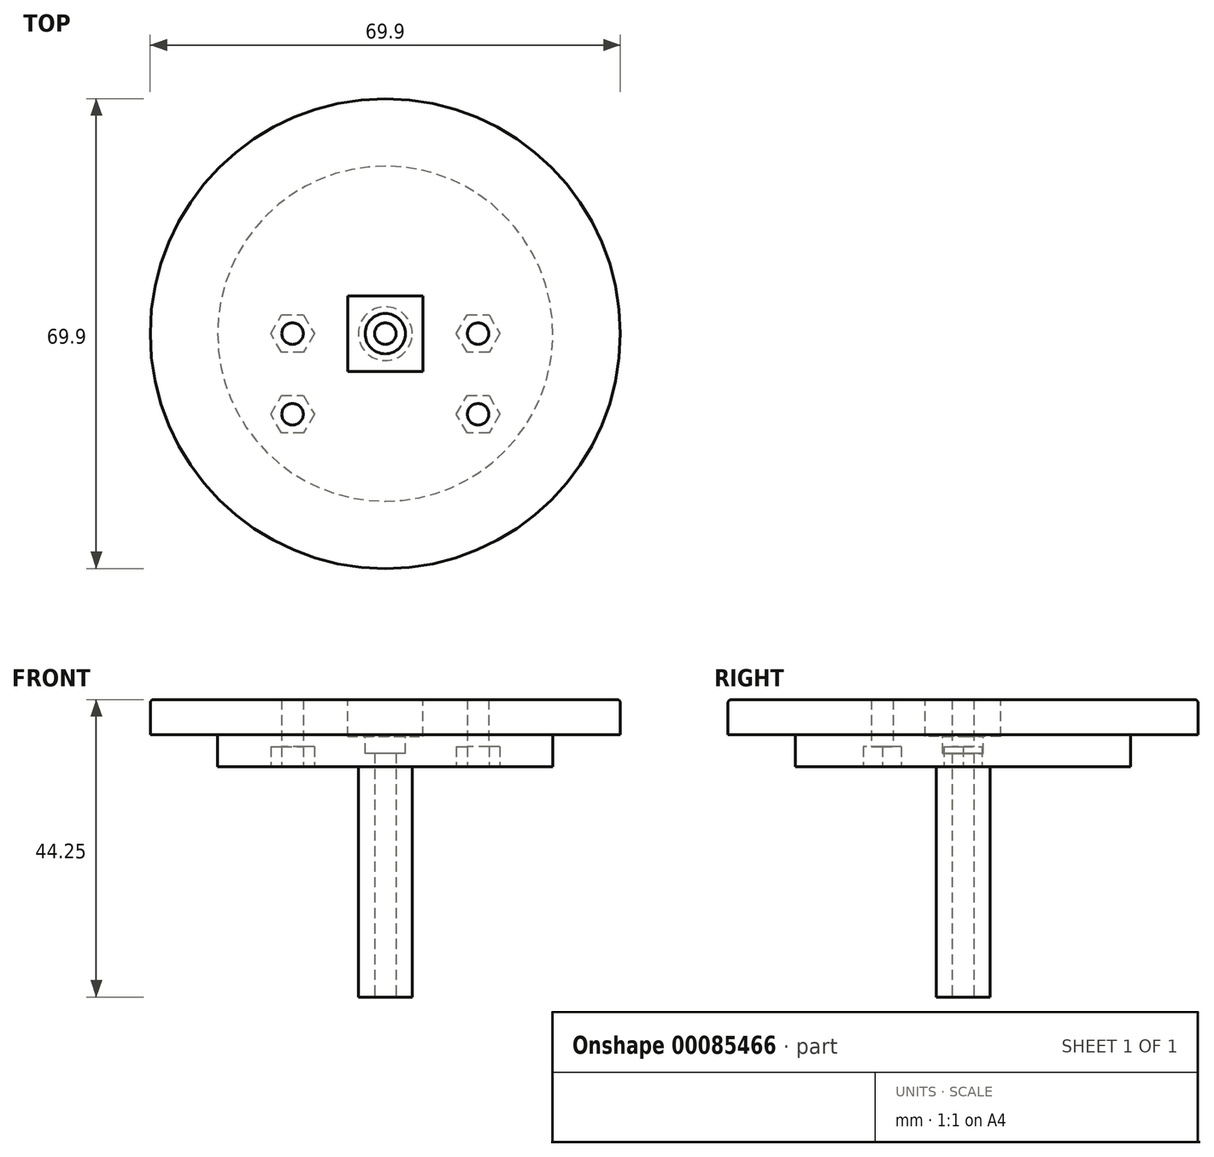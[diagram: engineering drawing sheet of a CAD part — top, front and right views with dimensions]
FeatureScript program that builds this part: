
annotation { "Feature Type Name" : "Feature", "Feature Type Description" : "" }
export const myFeature = defineFeature(function(context is Context, id is Id, definition is map)
    precondition{}
    {
        {
            var Q0;
            Q0=qCreatedBy(makeId("Top.planeOp"),FACE);
            var sketch = newSketch(context, id + "F0", { "sketchPlane" : qUnion([Q0])});
            skCircle(sketch, "E0", {"center": v(30.33, -8.57) * mm, "radius": 34.95 * mm});
            skLineSegment(sketch, "E1.bottom", {"start": v(35.93, -14.17) * mm, "end": v(24.73, -14.17) * mm});
            skLineSegment(sketch, "E1.top", {"start": v(35.93, -2.97) * mm, "end": v(24.73, -2.97) * mm});
            skLineSegment(sketch, "E1.left", {"start": v(35.93, -14.17) * mm, "end": v(35.93, -2.97) * mm});
            skLineSegment(sketch, "E1.right", {"start": v(24.73, -14.17) * mm, "end": v(24.73, -2.97) * mm});
            skPoint(sketch, "E2", {"position": v(24.73, -2.97) * mm});
            skLineSegment(sketch, "E3", {"start": v(30.33, -8.57) * mm, "end": v(5.62, -33.29) * mm, "construction": true});
            skLineSegment(sketch, "E4", {"start": v(30.33, -8.57) * mm, "end": v(55.05, 16.14) * mm, "construction": true});
            skCircle(sketch, "E5", {"center": v(30.33, -8.57) * mm, "radius": 24.93 * mm});
            skLineSegment(sketch, "E6", {"start": v(24.73, -14.17) * mm, "end": v(24.73, -43.07) * mm, "construction": true});
            skLineSegment(sketch, "E7", {"start": v(35.93, -14.17) * mm, "end": v(35.93, -43.07) * mm, "construction": true});
            skPoint(sketch, "E8", {"position": v(16.53, -20.57) * mm});
            skPoint(sketch, "E9", {"position": v(16.53, -8.57) * mm});
            skPoint(sketch, "E10", {"position": v(44.13, -8.57) * mm});
            skPoint(sketch, "E11", {"position": v(44.13, -20.57) * mm});
            skCircle(sketch, "E12.cCircle", {"center": v(16.53, -20.57) * mm, "radius": 3.23 * mm, "construction": true});
            skLineSegment(sketch, "E12.0", {"start": v(19.77, -20.57) * mm, "end": v(18.15, -23.37) * mm});
            skLineSegment(sketch, "E12.1", {"start": v(18.15, -23.37) * mm, "end": v(14.92, -23.37) * mm});
            skLineSegment(sketch, "E12.2", {"start": v(14.92, -23.37) * mm, "end": v(13.3, -20.57) * mm});
            skLineSegment(sketch, "E12.3", {"start": v(13.3, -20.57) * mm, "end": v(14.92, -17.77) * mm});
            skLineSegment(sketch, "E12.4", {"start": v(14.92, -17.77) * mm, "end": v(18.15, -17.77) * mm});
            skLineSegment(sketch, "E12.5", {"start": v(18.15, -17.77) * mm, "end": v(19.77, -20.57) * mm});
            skCircle(sketch, "E13.cCircle", {"center": v(16.53, -8.57) * mm, "radius": 3.23 * mm, "construction": true});
            skLineSegment(sketch, "E13.0", {"start": v(13.3, -8.57) * mm, "end": v(14.92, -5.77) * mm});
            skLineSegment(sketch, "E13.1", {"start": v(14.92, -5.77) * mm, "end": v(18.15, -5.77) * mm});
            skLineSegment(sketch, "E13.2", {"start": v(18.15, -5.77) * mm, "end": v(19.77, -8.57) * mm});
            skLineSegment(sketch, "E13.3", {"start": v(19.77, -8.57) * mm, "end": v(18.15, -11.37) * mm});
            skLineSegment(sketch, "E13.4", {"start": v(18.15, -11.37) * mm, "end": v(14.92, -11.37) * mm});
            skLineSegment(sketch, "E13.5", {"start": v(14.92, -11.37) * mm, "end": v(13.3, -8.57) * mm});
            skCircle(sketch, "E14.cCircle", {"center": v(44.13, -8.57) * mm, "radius": 3.23 * mm, "construction": true});
            skLineSegment(sketch, "E14.0", {"start": v(40.9, -8.57) * mm, "end": v(42.52, -5.77) * mm});
            skLineSegment(sketch, "E14.1", {"start": v(42.52, -5.77) * mm, "end": v(45.75, -5.77) * mm});
            skLineSegment(sketch, "E14.2", {"start": v(45.75, -5.77) * mm, "end": v(47.37, -8.57) * mm});
            skLineSegment(sketch, "E14.3", {"start": v(47.37, -8.57) * mm, "end": v(45.75, -11.37) * mm});
            skLineSegment(sketch, "E14.4", {"start": v(45.75, -11.37) * mm, "end": v(42.52, -11.37) * mm});
            skLineSegment(sketch, "E14.5", {"start": v(42.52, -11.37) * mm, "end": v(40.9, -8.57) * mm});
            skCircle(sketch, "E15.cCircle", {"center": v(44.13, -20.57) * mm, "radius": 3.23 * mm, "construction": true});
            skLineSegment(sketch, "E15.0", {"start": v(47.37, -20.57) * mm, "end": v(45.75, -23.37) * mm});
            skLineSegment(sketch, "E15.1", {"start": v(45.75, -23.37) * mm, "end": v(42.52, -23.37) * mm});
            skLineSegment(sketch, "E15.2", {"start": v(42.52, -23.37) * mm, "end": v(40.9, -20.57) * mm});
            skLineSegment(sketch, "E15.3", {"start": v(40.9, -20.57) * mm, "end": v(42.52, -17.77) * mm});
            skLineSegment(sketch, "E15.4", {"start": v(42.52, -17.77) * mm, "end": v(45.75, -17.77) * mm});
            skLineSegment(sketch, "E15.5", {"start": v(45.75, -17.77) * mm, "end": v(47.37, -20.57) * mm});
            skLineSegment(sketch, "E16", {"start": v(16.53, -8.57) * mm, "end": v(44.13, -8.57) * mm, "construction": true});
            skLineSegment(sketch, "E17", {"start": v(16.53, -20.57) * mm, "end": v(44.13, -20.57) * mm, "construction": true});
            skLineSegment(sketch, "E18", {"start": v(16.53, -8.57) * mm, "end": v(16.53, -20.57) * mm, "construction": true});
            skLineSegment(sketch, "E19", {"start": v(44.13, -20.57) * mm, "end": v(44.13, -8.57) * mm, "construction": true});
            skLineSegment(sketch, "E20", {"start": v(30.33, -20.57) * mm, "end": v(30.33, -8.57) * mm, "construction": true});
            skLineSegment(sketch, "E21", {"start": v(30.33, -8.57) * mm, "end": v(24.73, -8.57) * mm, "construction": true});
            skLineSegment(sketch, "E22", {"start": v(24.73, -8.57) * mm, "end": v(24.73, -20.57) * mm, "construction": true});
            skLineSegment(sketch, "E23", {"start": v(30.33, -8.57) * mm, "end": v(35.93, -8.57) * mm, "construction": true});
            skLineSegment(sketch, "E24", {"start": v(35.93, -8.57) * mm, "end": v(35.93, -20.57) * mm, "construction": true});
            skLineSegment(sketch, "E25", {"start": v(24.73, -8.57) * mm, "end": v(24.73, -14.17) * mm, "construction": true});
            skLineSegment(sketch, "E26", {"start": v(24.73, -8.57) * mm, "end": v(35.93, -8.57) * mm, "construction": true});
            skCircle(sketch, "E27", {"center": v(16.53, -8.57) * mm, "radius": 1.6 * mm});
            skCircle(sketch, "E28", {"center": v(44.13, -8.57) * mm, "radius": 1.6 * mm});
            skCircle(sketch, "E29", {"center": v(44.13, -20.57) * mm, "radius": 1.6 * mm});
            skCircle(sketch, "E30", {"center": v(16.53, -20.57) * mm, "radius": 1.6 * mm});
            skLineSegment(sketch, "E31", {"start": v(30.33, -8.57) * mm, "end": v(-4.62, -8.57) * mm, "construction": true});
            skCircle(sketch, "E32", {"center": v(30.33, -8.57) * mm, "radius": 1.6 * mm});
            skCircle(sketch, "E33", {"center": v(30.33, -8.57) * mm, "radius": 3 * mm});
            skSolve(sketch);
        }
        {
            var Q0;
            Q0=makeQuery(id+"F0.imprint","IMPRINT",FACE,{"disambiguationData":[TD([[makeQuery(id+"F0.imprint","IMPRINT",EDGE,{"derivedFrom":sQuery(id+"F0.wireOp",EDGE,"E0")}),1.0]])]});
            var Q1;
            Q1=makeQuery(id+"F0.imprint","IMPRINT",FACE,{"disambiguationData":[TD([[makeQuery(id+"F0.imprint","IMPRINT",EDGE,{"derivedFrom":sQuery(id+"F0.wireOp",EDGE,"is0V2jlH-Q4Ok-4M3Y-3QFo-iMKSAwjIWmyG.bottom")}),-1.0]])]});
            var Q2;
            Q2=makeQuery(id+"F0.imprint","IMPRINT",FACE,{"disambiguationData":[TD([[makeQuery(id+"F0.imprint","IMPRINT",EDGE,{"derivedFrom":sQuery(id+"F0.wireOp",EDGE,"E1.bottom")}),1.0]])]});
            var Q3;
            {var subQ5=sQuery(id+"F0.wireOp",EDGE,"is0V2jlH-Q4Ok-4M3Y-3QFo-iMKSAwjIWmyG.top");Q3=makeQuery(id+"F0.imprint","IMPRINT",FACE,{"disambiguationData":[TD([[makeQuery(id+"F0.imprint","IMPRINT",EDGE,{"derivedFrom":subQ5}),1.0]])]});}
            var Q4;
            Q4=makeQuery(id+"F0.imprint","IMPRINT",FACE,{"disambiguationData":[TD([[makeQuery(id+"F0.imprint","IMPRINT",EDGE,{"derivedFrom":sQuery(id+"F0.wireOp",EDGE,"E14.0")}),-1.0]])]});
            var Q5;
            {var subQ0=sQuery(id+"F0.wireOp",EDGE,"E15.3");Q5=makeQuery(id+"F0.imprint","IMPRINT",FACE,{"disambiguationData":[TD([[makeQuery(id+"F0.imprint","IMPRINT",EDGE,{"derivedFrom":subQ0}),-1.0]])]});}
            var Q6;
            {var subQ6=sQuery(id+"F0.wireOp",EDGE,"E15.0");Q6=makeQuery(id+"F0.imprint","IMPRINT",FACE,{"disambiguationData":[TD([[makeQuery(id+"F0.imprint","IMPRINT",EDGE,{"derivedFrom":subQ6}),-1.0]])]});}
            var Q7;
            {var subQ0=sQuery(id+"F0.wireOp",EDGE,"E12.4");Q7=makeQuery(id+"F0.imprint","IMPRINT",FACE,{"disambiguationData":[TD([[makeQuery(id+"F0.imprint","IMPRINT",EDGE,{"derivedFrom":subQ0}),-1.0]])]});}
            var Q8;
            {var subQ0=sQuery(id+"F0.wireOp",EDGE,"E12.1");Q8=makeQuery(id+"F0.imprint","IMPRINT",FACE,{"disambiguationData":[TD([[makeQuery(id+"F0.imprint","IMPRINT",EDGE,{"derivedFrom":subQ0}),-1.0]])]});}
            var Q9;
            Q9=makeQuery(id+"F0.imprint","IMPRINT",FACE,{"disambiguationData":[TD([[makeQuery(id+"F0.imprint","IMPRINT",EDGE,{"derivedFrom":sQuery(id+"F0.wireOp",EDGE,"E13.0")}),-1.0]])]});
            var Q10;
            Q10=makeQuery(id+"F0.imprint","IMPRINT",FACE,{"disambiguationData":[TD([[makeQuery(id+"F0.imprint","IMPRINT",EDGE,{"derivedFrom":sQuery(id+"F0.wireOp",EDGE,"E1.bottom")}),-1.0]])]});
            var Q11;
            Q11=makeQuery(id+"F0.imprint","IMPRINT",FACE,{"disambiguationData":[TD([[makeQuery(id+"F0.imprint","IMPRINT",EDGE,{"derivedFrom":sQuery(id+"F0.wireOp",EDGE,"E32")}),-1.0]])]});
            extrude(context, id + "F1", {"entities" : qUnion([Q0, Q1, Q2, Q3, Q4, Q5, Q6, Q7, Q8, Q9, Q10, Q11]), "depth" : 10 * mm});
        }
        {
            var Q0;
            Q0=makeQuery(id+"F1.opExtrude","CAP_EDGE",EDGE,{"disambiguationData":[OSD([sQuery(id+"F0.wireOp",EDGE,"E0")])],"isStart":false});
            fillet(context, id + "F2", {"entities" : qUnion([Q0]), "radius" : .5 * mm, "tangentPropagation" : true, "allowEdgeOverflow" : false});
        }
        {
            var Q0;
            Q0=makeQuery(id+"F0.imprint","IMPRINT",FACE,{"disambiguationData":[TD([[makeQuery(id+"F0.imprint","IMPRINT",EDGE,{"derivedFrom":sQuery(id+"F0.wireOp",EDGE,"E1.bottom")}),-1.0]])]});
            var Q1;
            {var subQ0=sQuery(id+"F0.wireOp",EDGE,"E12.1");Q1=makeQuery(id+"F0.imprint","IMPRINT",FACE,{"disambiguationData":[TD([[makeQuery(id+"F0.imprint","IMPRINT",EDGE,{"derivedFrom":subQ0}),-1.0]])]});}
            var Q2;
            {var subQ6=sQuery(id+"F0.wireOp",EDGE,"E15.0");Q2=makeQuery(id+"F0.imprint","IMPRINT",FACE,{"disambiguationData":[TD([[makeQuery(id+"F0.imprint","IMPRINT",EDGE,{"derivedFrom":subQ6}),-1.0]])]});}
            var Q3;
            Q3=makeQuery(id+"F1.opExtrude","CAP_FACE",FACE,{"disambiguationData":[OSD([sQuery(id+"F0.wireOp",EDGE,"E0"),sQuery(id+"F0.wireOp",EDGE,"E1.bottom"),sQuery(id+"F0.wireOp",EDGE,"E1.top"),sQuery(id+"F0.wireOp",EDGE,"E1.left"),sQuery(id+"F0.wireOp",EDGE,"E1.right")])],"isStart":false});
            var Q4;
            Q4=makeQuery(id+"F1.opExtrude","SWEPT_BODY",BODY,{"disambiguationData":[OSD([sQuery(id+"F0.wireOp",EDGE,"E0"),sQuery(id+"F0.wireOp",EDGE,"E1.bottom"),sQuery(id+"F0.wireOp",EDGE,"E1.top"),sQuery(id+"F0.wireOp",EDGE,"E1.left"),sQuery(id+"F0.wireOp",EDGE,"E1.right")])]});
            extrude(context, id + "F3", {"entities" : qUnion([Q0, Q1, Q2]), "operationType" : NewBodyOperationType.ADD, "endBoundEntityFace" : qUnion([Q3]), "endBoundEntityBody" : qUnion([Q4]), "depth" : 4.5 * mm});
        }
        {
            var Q0;
            Q0=makeQuery(id+"F0.imprint","IMPRINT",FACE,{"disambiguationData":[TD([[makeQuery(id+"F0.imprint","IMPRINT",EDGE,{"derivedFrom":sQuery(id+"F0.wireOp",EDGE,"E0")}),1.0]])]});
            extrude(context, id + "F4", {"entities" : qUnion([Q0]), "operationType" : NewBodyOperationType.REMOVE, "depth" : 4.75 * mm});
        }
        {
            var Q0;
            {var subQ0=sQuery(id+"F0.wireOp",EDGE,"E1.right");var subQ1=sQuery(id+"F0.wireOp",EDGE,"E1.left");var subQ2=sQuery(id+"F0.wireOp",EDGE,"E1.top");var subQ3=sQuery(id+"F0.wireOp",EDGE,"E1.bottom");Q0=makeQuery(id+"F3.boolean.opBoolean","MERGE",FACE,{"derivedFrom":[makeQuery(id+"F1.opExtrude","CAP_FACE",FACE,{"disambiguationData":[OSD([sQuery(id+"F0.wireOp",EDGE,"E0"),subQ3,subQ2,subQ1,subQ0])],"isStart":true}),makeQuery(id+"F3.opExtrude","CAP_FACE",FACE,{"disambiguationData":[OSD([subQ3,subQ2,subQ1,subQ0])],"isStart":true})]});}
            var sketch = newSketch(context, id + "F5", { "sketchPlane" : qUnion([Q0])});
            skLineSegment(sketch, "E34", {"start": v(30.33, 33.5) * mm, "end": v(30.33, -16.35) * mm, "construction": true});
            skCircle(sketch, "E35", {"center": v(30.33, 8.57) * mm, "radius": 4 * mm});
            skCircle(sketch, "E36", {"center": v(30.33, 8.57) * mm, "radius": 1.6 * mm});
            skSolve(sketch);
        }
        {
            var Q0;
            Q0=makeQuery(id+"F5.imprint","IMPRINT",FACE,{"disambiguationData":[TD([[makeQuery(id+"F5.imprint","IMPRINT",EDGE,{"derivedFrom":sQuery(id+"F5.wireOp",EDGE,"E35")}),1.0]])]});
            var Q1;
            Q1=makeQuery(id+"F0.imprint","IMPRINT",FACE,{"disambiguationData":[TD([[makeQuery(id+"F0.imprint","IMPRINT",EDGE,{"derivedFrom":sQuery(id+"F0.wireOp",EDGE,"E32")}),-1.0]])]});
            extrude(context, id + "F6", {"entities" : qUnion([Q0, Q1]), "operationType" : NewBodyOperationType.ADD, "depth" : 34.25 * mm});
        }
        {
            var Q0;
            {var subQ0=sQuery(id+"F0.wireOp",EDGE,"E15.2");Q0=makeQuery(id+"F0.imprint","IMPRINT",FACE,{"disambiguationData":[TD([[makeQuery(id+"F0.imprint","IMPRINT",EDGE,{"derivedFrom":subQ0}),-1.0]])]});}
            var Q1;
            {var subQ0=sQuery(id+"F0.wireOp",EDGE,"E15.1");var subQ1=sQuery(id+"F0.wireOp",EDGE,"E5");var subQ2=makeQuery(id+"F0.imprint","INTERSECT",VERTEX,{"derivedFrom":[subQ1,subQ0]});Q1=makeQuery(id+"F0.imprint","IMPRINT",FACE,{"disambiguationData":[TD([[makeQuery(id+"F0.imprint","IMPRINT",EDGE,{"disambiguationData":[TD([[subQ2,-1.0]])],"derivedFrom":subQ1}),-1.0]])]});}
            var Q2;
            Q2=makeQuery(id+"F0.imprint","IMPRINT",FACE,{"disambiguationData":[TD([[makeQuery(id+"F0.imprint","IMPRINT",EDGE,{"derivedFrom":sQuery(id+"F0.wireOp",EDGE,"E14.0")}),-1.0]])]});
            var Q3;
            Q3=makeQuery(id+"F0.imprint","IMPRINT",FACE,{"disambiguationData":[TD([[makeQuery(id+"F0.imprint","IMPRINT",EDGE,{"derivedFrom":sQuery(id+"F0.wireOp",EDGE,"E13.0")}),-1.0]])]});
            var Q4;
            {var subQ0=sQuery(id+"F0.wireOp",EDGE,"E12.1");var subQ1=sQuery(id+"F0.wireOp",EDGE,"E5");var subQ2=makeQuery(id+"F0.imprint","INTERSECT",VERTEX,{"derivedFrom":[subQ1,subQ0]});Q4=makeQuery(id+"F0.imprint","IMPRINT",FACE,{"disambiguationData":[TD([[makeQuery(id+"F0.imprint","IMPRINT",EDGE,{"disambiguationData":[TD([[subQ2,1.0]])],"derivedFrom":subQ1}),-1.0]])]});}
            var Q5;
            {var subQ5=sQuery(id+"F0.wireOp",EDGE,"E12.0");Q5=makeQuery(id+"F0.imprint","IMPRINT",FACE,{"disambiguationData":[TD([[makeQuery(id+"F0.imprint","IMPRINT",EDGE,{"derivedFrom":subQ5}),-1.0]])]});}
            extrude(context, id + "F7", {"entities" : qUnion([Q0, Q1, Q2, Q3, Q4, Q5]), "operationType" : NewBodyOperationType.REMOVE, "depth" : 3 * mm});
        }
        {
            var Q0;
            Q0=makeQuery(id+"F1.opExtrude","CAP_FACE",FACE,{"disambiguationData":[OSD([sQuery(id+"F0.wireOp",EDGE,"E0"),sQuery(id+"F0.wireOp",EDGE,"E27"),sQuery(id+"F0.wireOp",EDGE,"E28"),sQuery(id+"F0.wireOp",EDGE,"E29"),sQuery(id+"F0.wireOp",EDGE,"E30")])],"isStart":false});
            var sketch = newSketch(context, id + "F8", { "sketchPlane" : qUnion([Q0])});
            skLineSegment(sketch, "E37.bottom", {"start": v(24.73, -2.97) * mm, "end": v(35.93, -2.97) * mm});
            skLineSegment(sketch, "E37.top", {"start": v(24.73, -14.17) * mm, "end": v(35.93, -14.17) * mm});
            skLineSegment(sketch, "E37.left", {"start": v(24.73, -2.97) * mm, "end": v(24.73, -14.17) * mm});
            skLineSegment(sketch, "E37.right", {"start": v(35.93, -2.97) * mm, "end": v(35.93, -14.17) * mm});
            skPoint(sketch, "E37.middle", {"position": v(30.33, -8.57) * mm});
            skCircle(sketch, "E38", {"center": v(30.33, -8.57) * mm, "radius": 3 * mm});
            skSolve(sketch);
        }
        {
            var Q0;
            Q0=makeQuery(id+"F8.imprint","IMPRINT",FACE,{"disambiguationData":[TD([[makeQuery(id+"F8.imprint","IMPRINT",EDGE,{"derivedFrom":sQuery(id+"F8.wireOp",EDGE,"E37.bottom")}),-1.0]])]});
            var Q1;
            Q1=makeQuery(id+"F8.imprint","IMPRINT",FACE,{"disambiguationData":[TD([[makeQuery(id+"F8.imprint","IMPRINT",EDGE,{"derivedFrom":sQuery(id+"F8.wireOp",EDGE,"E38")}),1.0]])]});
            extrude(context, id + "F9", {"entities" : qUnion([Q0, Q1]), "operationType" : NewBodyOperationType.REMOVE, "oppositeDirection" : true, "depth" : 5.5 * mm});
        }
        {
            var Q0;
            Q0=makeQuery(id+"F0.imprint","IMPRINT",FACE,{"disambiguationData":[TD([[makeQuery(id+"F0.imprint","IMPRINT",EDGE,{"derivedFrom":sQuery(id+"F0.wireOp",EDGE,"E32")}),1.0]])]});
            extrude(context, id + "F10", {"entities" : qUnion([Q0]), "operationType" : NewBodyOperationType.REMOVE, "oppositeDirection" : true, "depth" : 35.94 * mm});
        }
        {
            var Q0;
            Q0=makeQuery(id+"F8.imprint","IMPRINT",FACE,{"disambiguationData":[TD([[makeQuery(id+"F8.imprint","IMPRINT",EDGE,{"derivedFrom":sQuery(id+"F8.wireOp",EDGE,"E38")}),1.0]])]});
            extrude(context, id + "F11", {"entities" : qUnion([Q0]), "operationType" : NewBodyOperationType.REMOVE, "oppositeDirection" : true, "depth" : 8 * mm});
        }
    });
